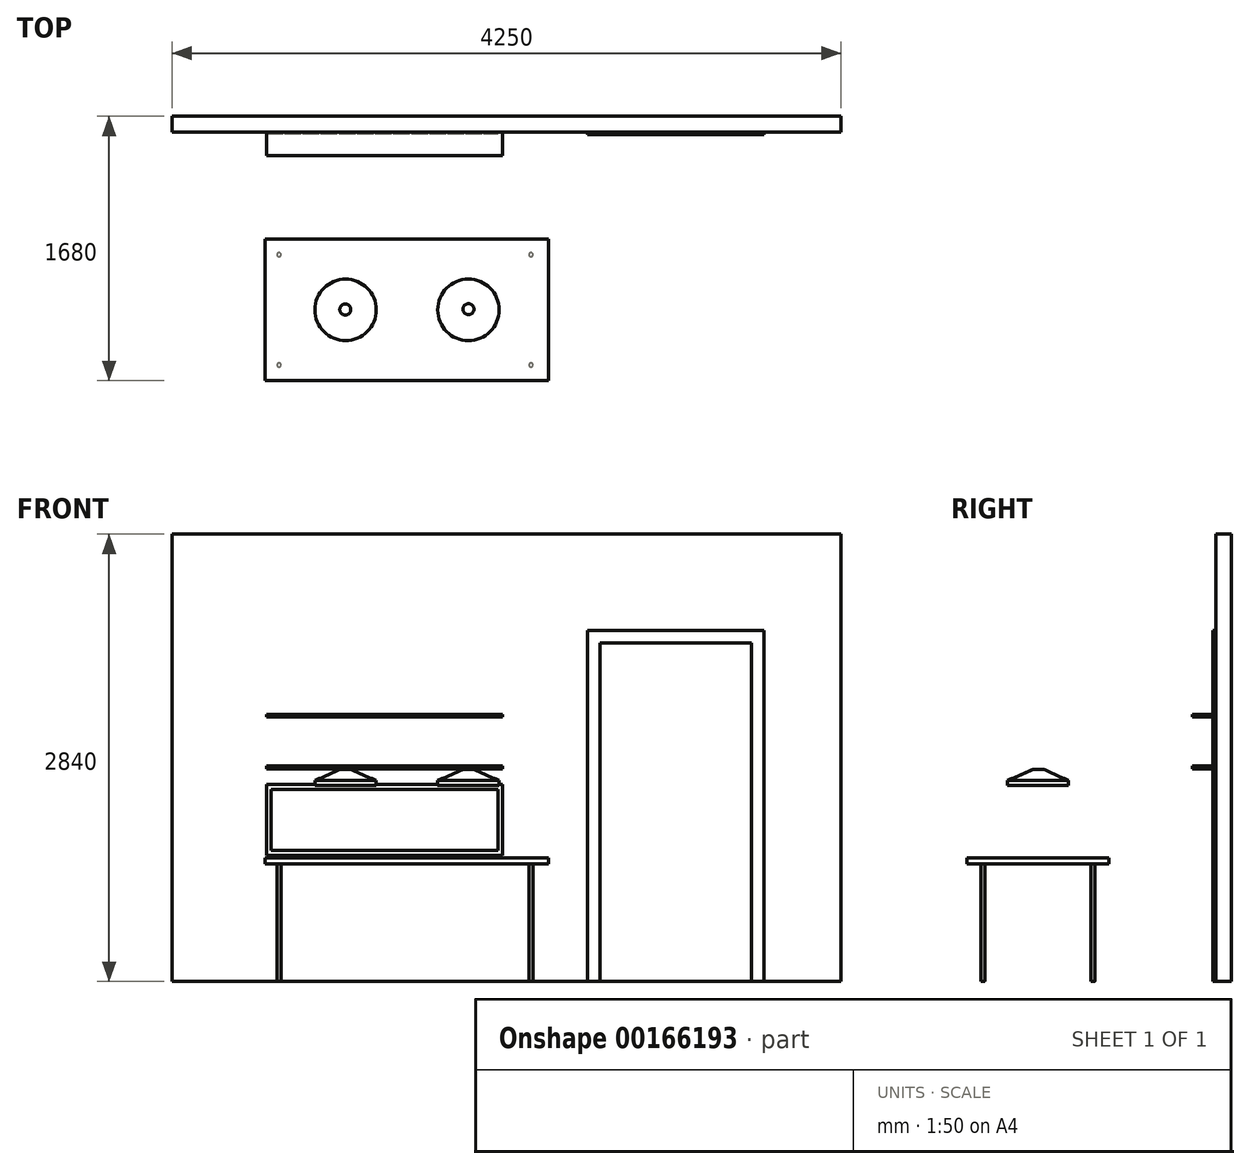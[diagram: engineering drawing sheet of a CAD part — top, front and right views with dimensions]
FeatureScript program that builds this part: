
annotation { "Feature Type Name" : "Feature", "Feature Type Description" : "" }
export const myFeature = defineFeature(function(context is Context, id is Id, definition is map)
    precondition{}
    {
        {
            var Q0;
            Q0=qCreatedBy(makeId("Front.planeOp"),FACE);
            var sketch = newSketch(context, id + "F0", { "sketchPlane" : qUnion([Q0])});
            skLineSegment(sketch, "E0.bottom", {"start": v(0, 0) * mm, "end": v(4250, 0) * mm});
            skLineSegment(sketch, "E0.top", {"start": v(0, 2840) * mm, "end": v(4250, 2840) * mm});
            skLineSegment(sketch, "E0.left", {"start": v(0, 0) * mm, "end": v(0, 2840) * mm});
            skLineSegment(sketch, "E0.right", {"start": v(4250, 0) * mm, "end": v(4250, 2840) * mm});
            skSolve(sketch);
        }
        {
            var Q0;
            Q0=makeQuery(id+"F0.imprint","IMPRINT",FACE,{"disambiguationData":[TD([[makeQuery(id+"F0.imprint","IMPRINT",EDGE,{"derivedFrom":sQuery(id+"F0.wireOp",EDGE,"E0.bottom")}),1.0]])]});
            extrude(context, id + "F1", {"entities" : qUnion([Q0]), "depth" : 100 * mm});
        }
        {
            var Q0;
            Q0=makeQuery(id+"F1.opExtrude","CAP_FACE",FACE,{"disambiguationData":[OSD([sQuery(id+"F0.wireOp",EDGE,"E0.bottom"),sQuery(id+"F0.wireOp",EDGE,"E0.top"),sQuery(id+"F0.wireOp",EDGE,"E0.left"),sQuery(id+"F0.wireOp",EDGE,"E0.right")])],"isStart":false});
            var sketch = newSketch(context, id + "F2", { "sketchPlane" : qUnion([Q0])});
            skLineSegment(sketch, "E1.bottom", {"start": v(3760, 0) * mm, "end": v(2640, 0) * mm});
            skLineSegment(sketch, "E1.top", {"start": v(3760, 2230) * mm, "end": v(2640, 2230) * mm});
            skLineSegment(sketch, "E1.left", {"start": v(3760, 0) * mm, "end": v(3760, 2230) * mm});
            skLineSegment(sketch, "E1.right", {"start": v(2640, 0) * mm, "end": v(2640, 2230) * mm});
            skSolve(sketch);
        }
        {
            var Q0;
            Q0=makeQuery(id+"F2.imprint","IMPRINT",FACE,{"disambiguationData":[TD([[makeQuery(id+"F2.imprint","IMPRINT",EDGE,{"derivedFrom":sQuery(id+"F2.wireOp",EDGE,"E1.bottom")}),1.0]])]});
            extrude(context, id + "F3", {"entities" : qUnion([Q0]), "depth" : 18 * mm});
        }
        {
            var Q0;
            Q0=makeQuery(id+"F3.opExtrude","CAP_FACE",FACE,{"disambiguationData":[OSD([sQuery(id+"F2.wireOp",EDGE,"E1.bottom"),sQuery(id+"F2.wireOp",EDGE,"E1.top"),sQuery(id+"F2.wireOp",EDGE,"E1.left"),sQuery(id+"F2.wireOp",EDGE,"E1.right")])],"isStart":false});
            var sketch = newSketch(context, id + "F4", { "sketchPlane" : qUnion([Q0])});
            skLineSegment(sketch, "E2.bottom", {"start": v(2720, 0) * mm, "end": v(3680, 0) * mm});
            skLineSegment(sketch, "E2.top", {"start": v(2720, 2150) * mm, "end": v(3680, 2150) * mm});
            skLineSegment(sketch, "E2.left", {"start": v(2720, 0) * mm, "end": v(2720, 2150) * mm});
            skLineSegment(sketch, "E2.right", {"start": v(3680, 0) * mm, "end": v(3680, 2150) * mm});
            skSolve(sketch);
        }
        {
            var Q0;
            Q0=makeQuery(id+"F4.imprint","IMPRINT",FACE,{"disambiguationData":[TD([[makeQuery(id+"F4.imprint","IMPRINT",EDGE,{"derivedFrom":sQuery(id+"F4.wireOp",EDGE,"E2.bottom")}),1.0]])]});
            var Q1;
            Q1=sQuery(id+"F4.wireOp",EDGE,"E2.top");
            var Q2;
            Q2=sQuery(id+"F4.wireOp",EDGE,"E2.right");
            var Q3;
            Q3=sQuery(id+"F4.wireOp",EDGE,"E2.left");
            var Q4;
            Q4=sQuery(id+"F4.wireOp",EDGE,"E2.bottom");
            extrude(context, id + "F5", {"entities" : qUnion([Q0]), "operationType" : NewBodyOperationType.REMOVE, "surfaceEntities" : qUnion([Q1, Q2, Q3, Q4]), "oppositeDirection" : true, "depth" : 5 * mm});
        }
        {
            var Q0;
            Q0=makeQuery(id+"F1.opExtrude","CAP_FACE",FACE,{"disambiguationData":[OSD([sQuery(id+"F0.wireOp",EDGE,"E0.bottom"),sQuery(id+"F0.wireOp",EDGE,"E0.top"),sQuery(id+"F0.wireOp",EDGE,"E0.left"),sQuery(id+"F0.wireOp",EDGE,"E0.right")])],"isStart":false});
            var sketch = newSketch(context, id + "F6", { "sketchPlane" : qUnion([Q0])});
            skLineSegment(sketch, "E3.bottom", {"start": v(600, 1368) * mm, "end": v(2100, 1368) * mm});
            skLineSegment(sketch, "E3.top", {"start": v(600, 1350) * mm, "end": v(2100, 1350) * mm});
            skLineSegment(sketch, "E3.left", {"start": v(600, 1368) * mm, "end": v(600, 1350) * mm});
            skLineSegment(sketch, "E3.right", {"start": v(2100, 1368) * mm, "end": v(2100, 1350) * mm});
            skLineSegment(sketch, "E4.bottom", {"start": v(600, 1696) * mm, "end": v(2100, 1696) * mm});
            skLineSegment(sketch, "E4.top", {"start": v(600, 1678) * mm, "end": v(2100, 1678) * mm});
            skLineSegment(sketch, "E4.left", {"start": v(600, 1696) * mm, "end": v(600, 1678) * mm});
            skLineSegment(sketch, "E4.right", {"start": v(2100, 1696) * mm, "end": v(2100, 1678) * mm});
            skSolve(sketch);
        }
        {
            var Q0;
            Q0=makeQuery(id+"F6.imprint","IMPRINT",FACE,{"disambiguationData":[TD([[makeQuery(id+"F6.imprint","IMPRINT",EDGE,{"derivedFrom":sQuery(id+"F6.wireOp",EDGE,"E4.bottom")}),-1.0]])]});
            var Q1;
            Q1=makeQuery(id+"F6.imprint","IMPRINT",FACE,{"disambiguationData":[TD([[makeQuery(id+"F6.imprint","IMPRINT",EDGE,{"derivedFrom":sQuery(id+"F6.wireOp",EDGE,"E3.bottom")}),-1.0]])]});
            extrude(context, id + "F7", {"entities" : qUnion([Q0, Q1]), "depth" : 150 * mm});
        }
        {
            var Q0;
            Q0=makeQuery(id+"F1.opExtrude","CAP_FACE",FACE,{"disambiguationData":[OSD([sQuery(id+"F0.wireOp",EDGE,"E0.bottom"),sQuery(id+"F0.wireOp",EDGE,"E0.top"),sQuery(id+"F0.wireOp",EDGE,"E0.left"),sQuery(id+"F0.wireOp",EDGE,"E0.right")])],"isStart":false});
            var sketch = newSketch(context, id + "F8", { "sketchPlane" : qUnion([Q0])});
            skLineSegment(sketch, "E5.bottom", {"start": v(600, 1250) * mm, "end": v(2100, 1250) * mm});
            skLineSegment(sketch, "E5.top", {"start": v(600, 800) * mm, "end": v(2100, 800) * mm});
            skLineSegment(sketch, "E5.left", {"start": v(600, 1250) * mm, "end": v(600, 800) * mm});
            skLineSegment(sketch, "E5.right", {"start": v(2100, 1250) * mm, "end": v(2100, 800) * mm});
            skSolve(sketch);
        }
        {
            var Q0;
            Q0=makeQuery(id+"F8.imprint","IMPRINT",FACE,{"disambiguationData":[TD([[makeQuery(id+"F8.imprint","IMPRINT",EDGE,{"derivedFrom":sQuery(id+"F8.wireOp",EDGE,"E5.bottom")}),-1.0]])]});
            var Q1;
            Q1=sQuery(id+"F8.wireOp",EDGE,"E5.bottom");
            extrude(context, id + "F9", {"entities" : qUnion([Q0]), "surfaceEntities" : qUnion([Q1]), "depth" : 10 * mm});
        }
        {
            var Q0;
            Q0=qCreatedBy(makeId("Top.planeOp"),FACE);
            var sketch = newSketch(context, id + "F10", { "sketchPlane" : qUnion([Q0])});
            skCircle(sketch, "E6", {"center": v(680, -1580) * mm, "radius": 12.5 * mm});
            skCircle(sketch, "E7", {"center": v(680, -880) * mm, "radius": 12.5 * mm});
            skCircle(sketch, "E8", {"center": v(2280, -1580) * mm, "radius": 12.5 * mm});
            skCircle(sketch, "E9", {"center": v(2280, -880) * mm, "radius": 12.5 * mm});
            skSolve(sketch);
        }
        {
            var Q0;
            Q0=makeQuery(id+"F10.imprint","IMPRINT",FACE,{"disambiguationData":[TD([[makeQuery(id+"F10.imprint","IMPRINT",EDGE,{"derivedFrom":sQuery(id+"F10.wireOp",EDGE,"E7")}),1.0]])]});
            var Q1;
            Q1=makeQuery(id+"F10.imprint","IMPRINT",FACE,{"disambiguationData":[TD([[makeQuery(id+"F10.imprint","IMPRINT",EDGE,{"derivedFrom":sQuery(id+"F10.wireOp",EDGE,"E9")}),1.0]])]});
            var Q2;
            Q2=makeQuery(id+"F10.imprint","IMPRINT",FACE,{"disambiguationData":[TD([[makeQuery(id+"F10.imprint","IMPRINT",EDGE,{"derivedFrom":sQuery(id+"F10.wireOp",EDGE,"E8")}),1.0]])]});
            var Q3;
            Q3=makeQuery(id+"F10.imprint","IMPRINT",FACE,{"disambiguationData":[TD([[makeQuery(id+"F10.imprint","IMPRINT",EDGE,{"derivedFrom":sQuery(id+"F10.wireOp",EDGE,"E6")}),1.0]])]});
            extrude(context, id + "F11", {"entities" : qUnion([Q0, Q1, Q2, Q3]), "depth" : 745 * mm});
        }
        {
            var Q0;
            Q0=makeQuery(id+"F11.opExtrude","CAP_FACE",FACE,{"disambiguationData":[OSD([sQuery(id+"F10.wireOp",EDGE,"E6")])],"isStart":false});
            var sketch = newSketch(context, id + "F12", { "sketchPlane" : qUnion([Q0])});
            skLineSegment(sketch, "E10.bottom", {"start": v(592.5, -780) * mm, "end": v(2392.5, -780) * mm});
            skLineSegment(sketch, "E10.top", {"start": v(592.5, -1680) * mm, "end": v(2392.5, -1680) * mm});
            skLineSegment(sketch, "E10.left", {"start": v(592.5, -780) * mm, "end": v(592.5, -1680) * mm});
            skLineSegment(sketch, "E10.right", {"start": v(2392.5, -780) * mm, "end": v(2392.5, -1680) * mm});
            skSolve(sketch);
        }
        {
            var Q0;
            Q0=makeQuery(id+"F12.imprint","IMPRINT",FACE,{"disambiguationData":[TD([[makeQuery(id+"F12.imprint","IMPRINT",EDGE,{"derivedFrom":sQuery(id+"F12.wireOp",EDGE,"E10.bottom")}),-1.0]])]});
            var Q1;
            Q1=makeQuery(id+"F12.imprint","IMPRINT",FACE,{"disambiguationData":[TD([[makeQuery(id+"F12.imprint","IMPRINT",EDGE,{"derivedFrom":makeQuery(id+"F11.opExtrude","CAP_EDGE",EDGE,{"disambiguationData":[OSD([sQuery(id+"F10.wireOp",EDGE,"E6")])],"isStart":false})}),1.0]])]});
            extrude(context, id + "F13", {"entities" : qUnion([Q0, Q1]), "depth" : 40 * mm});
        }
        {
            var Q0;
            Q0=makeQuery(id+"F9.opExtrude","CAP_FACE",FACE,{"disambiguationData":[OSD([sQuery(id+"F8.wireOp",EDGE,"E5.bottom"),sQuery(id+"F8.wireOp",EDGE,"E5.top"),sQuery(id+"F8.wireOp",EDGE,"E5.left"),sQuery(id+"F8.wireOp",EDGE,"E5.right")])],"isStart":false});
            var sketch = newSketch(context, id + "F14", { "sketchPlane" : qUnion([Q0])});
            skLineSegment(sketch, "E11.bottom", {"start": v(630, 1220) * mm, "end": v(2070, 1220) * mm});
            skLineSegment(sketch, "E11.top", {"start": v(630, 830) * mm, "end": v(2070, 830) * mm});
            skLineSegment(sketch, "E11.left", {"start": v(630, 1220) * mm, "end": v(630, 830) * mm});
            skLineSegment(sketch, "E11.right", {"start": v(2070, 1220) * mm, "end": v(2070, 830) * mm});
            skSolve(sketch);
        }
        {
            var Q0;
            Q0=makeQuery(id+"F14.imprint","IMPRINT",FACE,{"disambiguationData":[TD([[makeQuery(id+"F14.imprint","IMPRINT",EDGE,{"derivedFrom":sQuery(id+"F14.wireOp",EDGE,"E11.bottom")}),-1.0]])]});
            extrude(context, id + "F15", {"entities" : qUnion([Q0]), "depth" : 2 * mm});
        }
        {
            var Q0;
            Q0=makeQuery(id+"F13.opExtrude","CAP_FACE",FACE,{"disambiguationData":[OSD([sQuery(id+"F12.wireOp",EDGE,"E10.bottom"),sQuery(id+"F12.wireOp",EDGE,"E10.top"),sQuery(id+"F12.wireOp",EDGE,"E10.left"),sQuery(id+"F12.wireOp",EDGE,"E10.right")])],"isStart":false});
            cPlane(context, id + "F16", {"entities" : qUnion([Q0]), "cplaneType" : CPlaneType.OFFSET, "offset" : 460 * mm, "width" : 150 * mm, "height" : 150 * mm});
        }
        {
            var Q0;
            Q0=qCreatedBy(id+"F16.planeOp",FACE);
            var sketch = newSketch(context, id + "F17", { "sketchPlane" : qUnion([Q0])});
            skCircle(sketch, "E12", {"center": v(1102.5, -1230) * mm, "radius": 195 * mm});
            skCircle(sketch, "E13", {"center": v(1882.5, -1230) * mm, "radius": 195 * mm});
            skSolve(sketch);
        }
        {
            var Q0;
            Q0=makeQuery(id+"F17.imprint","IMPRINT",FACE,{"disambiguationData":[TD([[makeQuery(id+"F17.imprint","IMPRINT",EDGE,{"derivedFrom":sQuery(id+"F17.wireOp",EDGE,"E12")}),1.0]])]});
            var Q1;
            Q1=makeQuery(id+"F17.imprint","IMPRINT",FACE,{"disambiguationData":[TD([[makeQuery(id+"F17.imprint","IMPRINT",EDGE,{"derivedFrom":sQuery(id+"F17.wireOp",EDGE,"E13")}),1.0]])]});
            extrude(context, id + "F18", {"entities" : qUnion([Q0, Q1]), "depth" : 30 * mm});
        }
        {
            var Q0;
            Q0=makeQuery(id+"F18.opExtrude","CAP_FACE",FACE,{"disambiguationData":[OSD([sQuery(id+"F17.wireOp",EDGE,"E13")])],"isStart":false});
            var sketch = newSketch(context, id + "F19", { "sketchPlane" : qUnion([Q0])});
            skCircle(sketch, "E14", {"center": v(1882.5, -1230) * mm, "radius": 195 * mm});
            skSolve(sketch);
        }
        {
            var Q0;
            Q0=makeQuery(id+"F19.imprint","IMPRINT",FACE,{"disambiguationData":[TD([[makeQuery(id+"F19.imprint","IMPRINT",EDGE,{"derivedFrom":sQuery(id+"F19.wireOp",EDGE,"E14")}),1.0]])]});
            cPlane(context, id + "F20", {"entities" : qUnion([Q0]), "cplaneType" : CPlaneType.OFFSET, "offset" : 70 * mm, "width" : 150 * mm, "height" : 150 * mm});
        }
        {
            var Q0;
            Q0=qCreatedBy(id+"F20.planeOp",FACE);
            var sketch = newSketch(context, id + "F21", { "sketchPlane" : qUnion([Q0])});
            skCircle(sketch, "E15", {"center": v(1883.03, -1225.8) * mm, "radius": 35 * mm});
            skSolve(sketch);
        }
        {
            var Q0;
            Q0=makeQuery(id+"F19.imprint","IMPRINT",FACE,{"disambiguationData":[TD([[makeQuery(id+"F19.imprint","IMPRINT",EDGE,{"derivedFrom":sQuery(id+"F19.wireOp",EDGE,"E14")}),1.0]])]});
            var Q1;
            Q1=makeQuery(id+"F21.imprint","IMPRINT",FACE,{"disambiguationData":[TD([[makeQuery(id+"F21.imprint","IMPRINT",EDGE,{"derivedFrom":sQuery(id+"F21.wireOp",EDGE,"E15")}),1.0]])]});
            loft(context, id + "F22", {"sheetProfilesArray" : [{ "sheetProfileEntities" : qUnion([Q0]) }, { "sheetProfileEntities" : qUnion([Q1]) }]});
        }
        {
            var Q0;
            Q0=makeQuery(id+"F18.opExtrude","CAP_FACE",FACE,{"disambiguationData":[OSD([sQuery(id+"F17.wireOp",EDGE,"E12")])],"isStart":false});
            var sketch = newSketch(context, id + "F23", { "sketchPlane" : qUnion([Q0])});
            skCircle(sketch, "E16", {"center": v(1102.5, -1230) * mm, "radius": 195 * mm});
            skSolve(sketch);
        }
        {
            var Q0;
            Q0=qCreatedBy(id+"F20.planeOp",FACE);
            var sketch = newSketch(context, id + "F24", { "sketchPlane" : qUnion([Q0])});
            skCircle(sketch, "E17", {"center": v(1100.6, -1228.04) * mm, "radius": 35 * mm});
            skSolve(sketch);
        }
        {
            var Q0;
            Q0=makeQuery(id+"F23.imprint","IMPRINT",FACE,{"disambiguationData":[TD([[makeQuery(id+"F23.imprint","IMPRINT",EDGE,{"derivedFrom":sQuery(id+"F23.wireOp",EDGE,"E16")}),1.0]])]});
            var Q1;
            Q1=makeQuery(id+"F24.imprint","IMPRINT",FACE,{"disambiguationData":[TD([[makeQuery(id+"F24.imprint","IMPRINT",EDGE,{"derivedFrom":sQuery(id+"F24.wireOp",EDGE,"E17")}),1.0]])]});
            loft(context, id + "F25", {"sheetProfilesArray" : [{ "sheetProfileEntities" : qUnion([Q0]) }, { "sheetProfileEntities" : qUnion([Q1]) }]});
        }
    });
